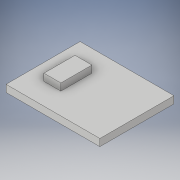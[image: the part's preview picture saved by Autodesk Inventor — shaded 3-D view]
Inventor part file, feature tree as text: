
AUTODESK INVENTOR PART (.ipt)
format: ipt  version: 2019 (Build 230136000, 136)  size: 104,448 bytes
history: native  units: mm
features: extrude x2, sketch x2, other x1
ambient origin geometry x8: Origin, YZ Plane, XZ Plane, XY Plane, X Axis, Y Axis, Z Axis, Center Point
bodies: Body1 (feature_tree)
feature tree (5):
  other  "Bryła1"
  extrude  "Wyciągnięcie proste1"  Depth=10.5mm
  extrude  "Wyciągnięcie proste2"  Depth=5.25mm
  sketch  "Szkic1"
  sketch  "Szkic2"
